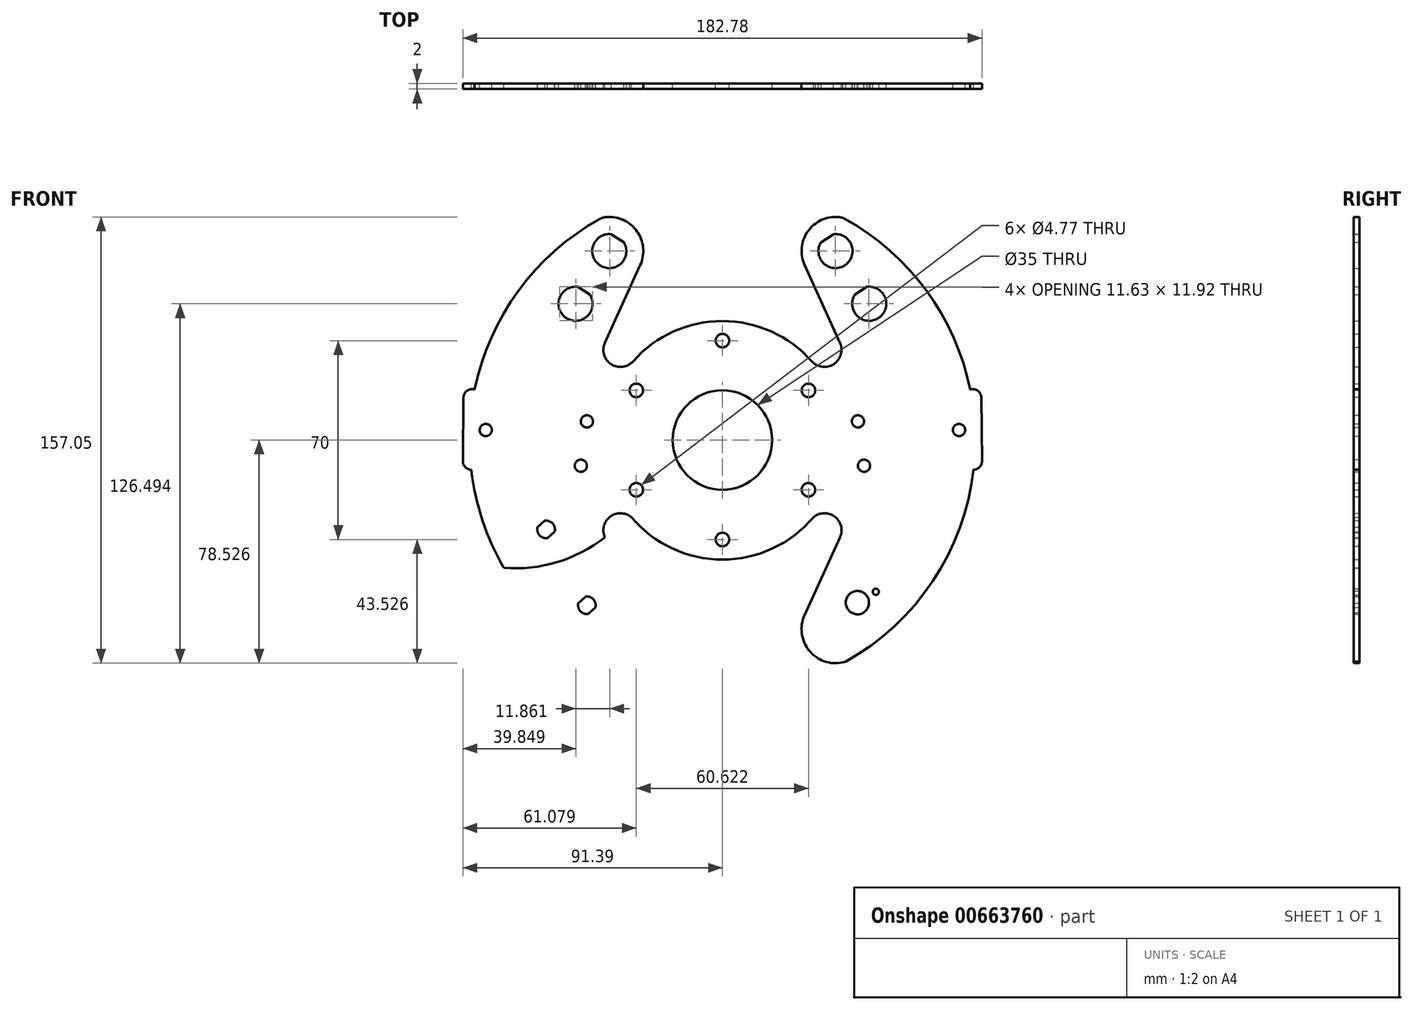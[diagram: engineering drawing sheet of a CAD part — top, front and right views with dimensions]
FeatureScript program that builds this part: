
annotation { "Feature Type Name" : "Feature", "Feature Type Description" : "" }
export const myFeature = defineFeature(function(context is Context, id is Id, definition is map)
    precondition{}
    {
        {
            var Q0;
            Q0=qCreatedBy(makeId("Front.planeOp"), FACE);
            var sketch = newSketch(context, id + "F0", { "sketchPlane" : qUnion([Q0])});
            skCircle(sketch, "E0", {"center": v(1.67, 27.2) * mm, "radius": 2.38 * mm});
            skCircle(sketch, "E1", {"center": v(1.67, -42.8) * mm, "radius": 2.38 * mm});
            skCircle(sketch, "E2.1.0", {"center": v(31.98, 9.7) * mm, "radius": 2.38 * mm});
            skCircle(sketch, "E2.2.0", {"center": v(31.98, -25.3) * mm, "radius": 2.38 * mm});
            skCircle(sketch, "E2.4.0", {"center": v(-28.64, -25.3) * mm, "radius": 2.38 * mm});
            skCircle(sketch, "E2.5.0", {"center": v(-28.64, 9.7) * mm, "radius": 2.38 * mm});
            skPoint(sketch, "E2.center", {"position": v(1.67, -7.8) * mm});
            skLineSegment(sketch, "E2.anchor1", {"start": v(1.67, -7.8) * mm, "end": v(1.67, 27.2) * mm, "construction": true});
            skLineSegment(sketch, "E2.anchor2", {"start": v(1.67, -7.8) * mm, "end": v(-28.64, 9.7) * mm, "construction": true});
            skCircle(sketch, "E3", {"center": v(1.67, -7.8) * mm, "radius": 17.5 * mm});
            skArc(sketch, "E4", {"start": v(-27.27, 53.76) * mm, "mid": v(-28.4, 65.68) * mm, "end": v(-39.28, 70.68) * mm});
            skLineSegment(sketch, "E5", {"start": v(-27.27, 53.76) * mm, "end": v(-39.71, 26.43) * mm});
            skArc(sketch, "E6", {"start": v(-39.71, 26.43) * mm, "mid": v(-37.52, 18.9) * mm, "end": v(-29.76, 19.97) * mm});
            skLineSegment(sketch, "E7", {"start": v(1.67, -7.8) * mm, "end": v(1.67, 85.88) * mm, "construction": true});
            skLineSegment(sketch, "E8", {"start": v(1.67, -7.8) * mm, "end": v(1.67, -99.4) * mm, "construction": true});
            skLineSegment(sketch, "E9", {"start": v(1.67, -7.8) * mm, "end": v(-95.95, -7.8) * mm, "construction": true});
            skLineSegment(sketch, "E10", {"start": v(1.67, -7.8) * mm, "end": v(114.9, -7.8) * mm, "construction": true});
            skArc(sketch, "E11.MirrorCS", {"start": v(30.6, 53.76) * mm, "mid": v(31.74, 65.68) * mm, "end": v(42.62, 70.68) * mm});
            skLineSegment(sketch, "E12.MirrorCS", {"start": v(30.6, 53.76) * mm, "end": v(43.05, 26.43) * mm});
            skArc(sketch, "E13.MirrorCS", {"start": v(43.05, 26.43) * mm, "mid": v(40.86, 18.9) * mm, "end": v(33.1, 19.97) * mm});
            skArc(sketch, "E14.MirrorCS", {"start": v(-39.71, -42.02) * mm, "mid": v(-37.52, -34.5) * mm, "end": v(-29.76, -35.55) * mm});
            skArc(sketch, "E15.MirrorCS", {"start": v(30.6, -69.35) * mm, "mid": v(32.18, -81.85) * mm, "end": v(44.06, -86.05) * mm});
            skLineSegment(sketch, "E16.MirrorCS", {"start": v(30.6, -69.35) * mm, "end": v(43.05, -42.02) * mm});
            skArc(sketch, "E17.MirrorCS", {"start": v(43.05, -42.02) * mm, "mid": v(40.86, -34.5) * mm, "end": v(33.1, -35.55) * mm});
            skPoint(sketch, "E18.middle", {"position": v(114.9, -7.8) * mm});
            skCircle(sketch, "E19", {"center": v(49.37, -1.21) * mm, "radius": 2.15 * mm});
            skLineSegment(sketch, "E20", {"start": v(49.37, -1.21) * mm, "end": v(49.37, -16.96) * mm, "construction": true});
            skLineSegment(sketch, "E21", {"start": v(49.37, -1.21) * mm, "end": v(51.52, -16.82) * mm, "construction": true});
            skCircle(sketch, "E22", {"center": v(51.52, -16.82) * mm, "radius": 2.15 * mm});
            skLineSegment(sketch, "E23", {"start": v(50.44, -9.02) * mm, "end": v(84.97, -4.26) * mm, "construction": true});
            skCircle(sketch, "E24", {"center": v(84.97, -4.26) * mm, "radius": 2.15 * mm});
            skLineSegment(sketch, "E25", {"start": v(51.51, -1.08) * mm, "end": v(53.65, -16.52) * mm, "construction": true});
            skLineSegment(sketch, "E26", {"start": v(84.97, -4.26) * mm, "end": v(90.91, -3.44) * mm, "construction": true});
            skArc(sketch, "E27", {"start": v(88.88, 9.98) * mm, "mid": v(73.5, 44.76) * mm, "end": v(45, 69.95) * mm});
            skLineSegment(sketch, "E28.filletArc", {"start": v(90.06, -18.22) * mm, "end": v(90.06, -18.22) * mm});
            skCircle(sketch, "E29.MirrorC", {"center": v(-46.03, -1.21) * mm, "radius": 2.15 * mm});
            skCircle(sketch, "E30.MirrorC", {"center": v(-81.63, -4.26) * mm, "radius": 2.15 * mm});
            skCircle(sketch, "E31.MirrorC", {"center": v(-48.18, -16.82) * mm, "radius": 2.15 * mm});
            skArc(sketch, "E32", {"start": v(-86.72, -18.22) * mm, "mid": v(-82.8, -36.07) * mm, "end": v(-75.3, -52.74) * mm});
            skArc(sketch, "E33", {"start": v(-41.66, 69.95) * mm, "mid": v(-70.15, 44.76) * mm, "end": v(-85.54, 9.98) * mm});
            skArc(sketch, "E34", {"start": v(45.1, -85.78) * mm, "mid": v(75.73, -57.42) * mm, "end": v(90.06, -18.22) * mm});
            skLineSegment(sketch, "E35", {"start": v(45.1, -85.78) * mm, "end": v(45.1, -85.78) * mm});
            skArc(sketch, "E36", {"start": v(-30.39, -34.94) * mm, "mid": v(1.67, -49.82) * mm, "end": v(33.72, -34.94) * mm});
            skArc(sketch, "E37", {"start": v(33.1, 19.97) * mm, "mid": v(1.67, 34.12) * mm, "end": v(-29.76, 19.97) * mm});
            skLineSegment(sketch, "E38", {"start": v(33.1, 19.97) * mm, "end": v(33.1, 19.97) * mm});
            skCircle(sketch, "E39", {"center": v(49.19, -65) * mm, "radius": 4.09 * mm});
            skLineSegment(sketch, "E40", {"start": v(49.19, -65) * mm, "end": v(55.66, -61.17) * mm, "construction": true});
            skCircle(sketch, "E41", {"center": v(55.66, -61.17) * mm, "radius": 1.1 * mm});
            skLineSegment(sketch, "E42", {"start": v(-38.2, 58.73) * mm, "end": v(-50.01, 40.18) * mm, "construction": true});
            skPoint(sketch, "E43.visualSharp", {"position": v(-40.72, 70.46) * mm});
            skArc(sketch, "E43.filletArc", {"start": v(-39.28, 70.68) * mm, "mid": v(-40.5, 70.44) * mm, "end": v(-41.66, 69.95) * mm});
            skPoint(sketch, "E44.visualSharp", {"position": v(-27.27, 53.76) * mm});
            skLineSegment(sketch, "E44.filletArc", {"start": v(-27.27, 53.76) * mm, "end": v(-27.27, 53.76) * mm});
            skArc(sketch, "E45.filletArc", {"start": v(45, 69.95) * mm, "mid": v(43.84, 70.44) * mm, "end": v(42.62, 70.68) * mm});
            skPoint(sketch, "E46.visualSharp", {"position": v(30.6, 53.76) * mm});
            skLineSegment(sketch, "E46.filletArc", {"start": v(30.6, 53.76) * mm, "end": v(30.6, 53.76) * mm});
            skLineSegment(sketch, "E47", {"start": v(-38.2, 58.73) * mm, "end": v(-34.18, 65.02) * mm, "construction": true});
            skLineSegment(sketch, "E48", {"start": v(-37.47, 64.7) * mm, "end": v(-37.44, 64.68) * mm});
            skLineSegment(sketch, "E49", {"start": v(-37.44, 64.68) * mm, "end": v(-33.05, 61.88) * mm});
            skArc(sketch, "E50", {"start": v(-37.44, 64.68) * mm, "mid": v(-41.38, 53.66) * mm, "end": v(-33.05, 61.88) * mm});
            skCircle(sketch, "E51", {"center": v(-50.01, 40.18) * mm, "radius": 9.26 * mm, "construction": true});
            skCircle(sketch, "E52", {"center": v(-38.2, 58.73) * mm, "radius": 8.88 * mm, "construction": true});
            skArc(sketch, "E53.MirrorCS", {"start": v(40.78, 64.68) * mm, "mid": v(44.71, 53.66) * mm, "end": v(36.4, 61.88) * mm});
            skLineSegment(sketch, "E54.MirrorCS", {"start": v(40.78, 64.68) * mm, "end": v(36.4, 61.88) * mm});
            skCircle(sketch, "E55.MirrorC", {"center": v(41.53, 58.73) * mm, "radius": 8.88 * mm, "construction": true});
            skCircle(sketch, "E56.MirrorC", {"center": v(49.48, -66) * mm, "radius": 3.1 * mm});
            skLineSegment(sketch, "E57", {"start": v(-47.9, -64.11) * mm, "end": v(-46.5, -62.86) * mm});
            skLineSegment(sketch, "E58", {"start": v(-47.9, -64.11) * mm, "end": v(-49.04, -65.12) * mm});
            skLineSegment(sketch, "E59", {"start": v(-44.37, -67.9) * mm, "end": v(-42.96, -66.64) * mm});
            skLineSegment(sketch, "E60", {"start": v(-44.37, -67.9) * mm, "end": v(-45.6, -69) * mm});
            skArc(sketch, "E61", {"start": v(-49.04, -65.12) * mm, "mid": v(-48.36, -67.98) * mm, "end": v(-45.6, -69) * mm});
            skArc(sketch, "E62", {"start": v(-43.05, -66.72) * mm, "mid": v(-43.73, -63.86) * mm, "end": v(-46.5, -62.86) * mm});
            skLineSegment(sketch, "E63.MirrorCS", {"start": v(-86.72, -18.22) * mm, "end": v(-86.72, -18.22) * mm});
            skLineSegment(sketch, "E64", {"start": v(-89.72, -15.18) * mm, "end": v(-89.48, 7.16) * mm});
            skLineSegment(sketch, "E65", {"start": v(-85.54, 9.98) * mm, "end": v(-85.54, 9.98) * mm});
            skPoint(sketch, "E66.visualSharp", {"position": v(-89.43, 11.26) * mm});
            skArc(sketch, "E66.filletArc", {"start": v(-85.54, 9.98) * mm, "mid": v(-88.22, 9.57) * mm, "end": v(-89.48, 7.16) * mm});
            skPoint(sketch, "E67.visualSharp", {"position": v(-89.75, -18.22) * mm});
            skArc(sketch, "E67.filletArc", {"start": v(-89.72, -15.18) * mm, "mid": v(-88.85, -17.33) * mm, "end": v(-86.72, -18.22) * mm});
            skArc(sketch, "E68.MirrorCS", {"start": v(88.88, 9.98) * mm, "mid": v(91.56, 9.57) * mm, "end": v(92.82, 7.16) * mm});
            skLineSegment(sketch, "E69.MirrorCS", {"start": v(93.06, -15.18) * mm, "end": v(92.82, 7.16) * mm});
            skArc(sketch, "E70.MirrorCS", {"start": v(93.06, -15.18) * mm, "mid": v(92.2, -17.33) * mm, "end": v(90.06, -18.22) * mm});
            skLineSegment(sketch, "E71", {"start": v(44.06, -86.05) * mm, "end": v(45.1, -85.78) * mm});
            skLineSegment(sketch, "E72", {"start": v(-29.76, 19.97) * mm, "end": v(-29.76, 19.97) * mm});
            skArc(sketch, "E73", {"start": v(-49.3, 46.14) * mm, "mid": v(-53.24, 35.12) * mm, "end": v(-44.91, 43.34) * mm});
            skLineSegment(sketch, "E74", {"start": v(-49.3, 46.14) * mm, "end": v(-44.91, 43.34) * mm});
            skLineSegment(sketch, "E75.MirrorCS", {"start": v(52.64, 46.14) * mm, "end": v(48.25, 43.34) * mm});
            skArc(sketch, "E76.MirrorCS", {"start": v(52.64, 46.14) * mm, "mid": v(56.58, 35.12) * mm, "end": v(48.25, 43.34) * mm});
            skArc(sketch, "E77", {"start": v(-75.3, -52.74) * mm, "mid": v(-56.5, -50.75) * mm, "end": v(-39.71, -42.02) * mm});
            skLineSegment(sketch, "E78", {"start": v(-62.26, -37.42) * mm, "end": v(-60.85, -36.16) * mm});
            skLineSegment(sketch, "E79", {"start": v(-62.26, -37.42) * mm, "end": v(-63.4, -38.43) * mm});
            skLineSegment(sketch, "E80", {"start": v(-58.73, -41.2) * mm, "end": v(-57.32, -39.95) * mm});
            skLineSegment(sketch, "E81", {"start": v(-58.73, -41.2) * mm, "end": v(-59.96, -42.3) * mm});
            skArc(sketch, "E82", {"start": v(-63.4, -38.43) * mm, "mid": v(-62.72, -41.29) * mm, "end": v(-59.96, -42.3) * mm});
            skArc(sketch, "E83", {"start": v(-57.4, -40.03) * mm, "mid": v(-58.09, -37.17) * mm, "end": v(-60.85, -36.16) * mm});
            skLineSegment(sketch, "E84", {"start": v(-41.76, -85.78) * mm, "end": v(-41.76, -85.78) * mm});
            skSolve(sketch);
        }
        {
            var Q0;
            Q0 = qSketchRegion(id + "F0", true);
            extrude(context, id + "F1", {"entities" : qUnion([Q0]), "depth" : 2 * mm, "offsetDistance" : 25 * mm});
        }
    });
